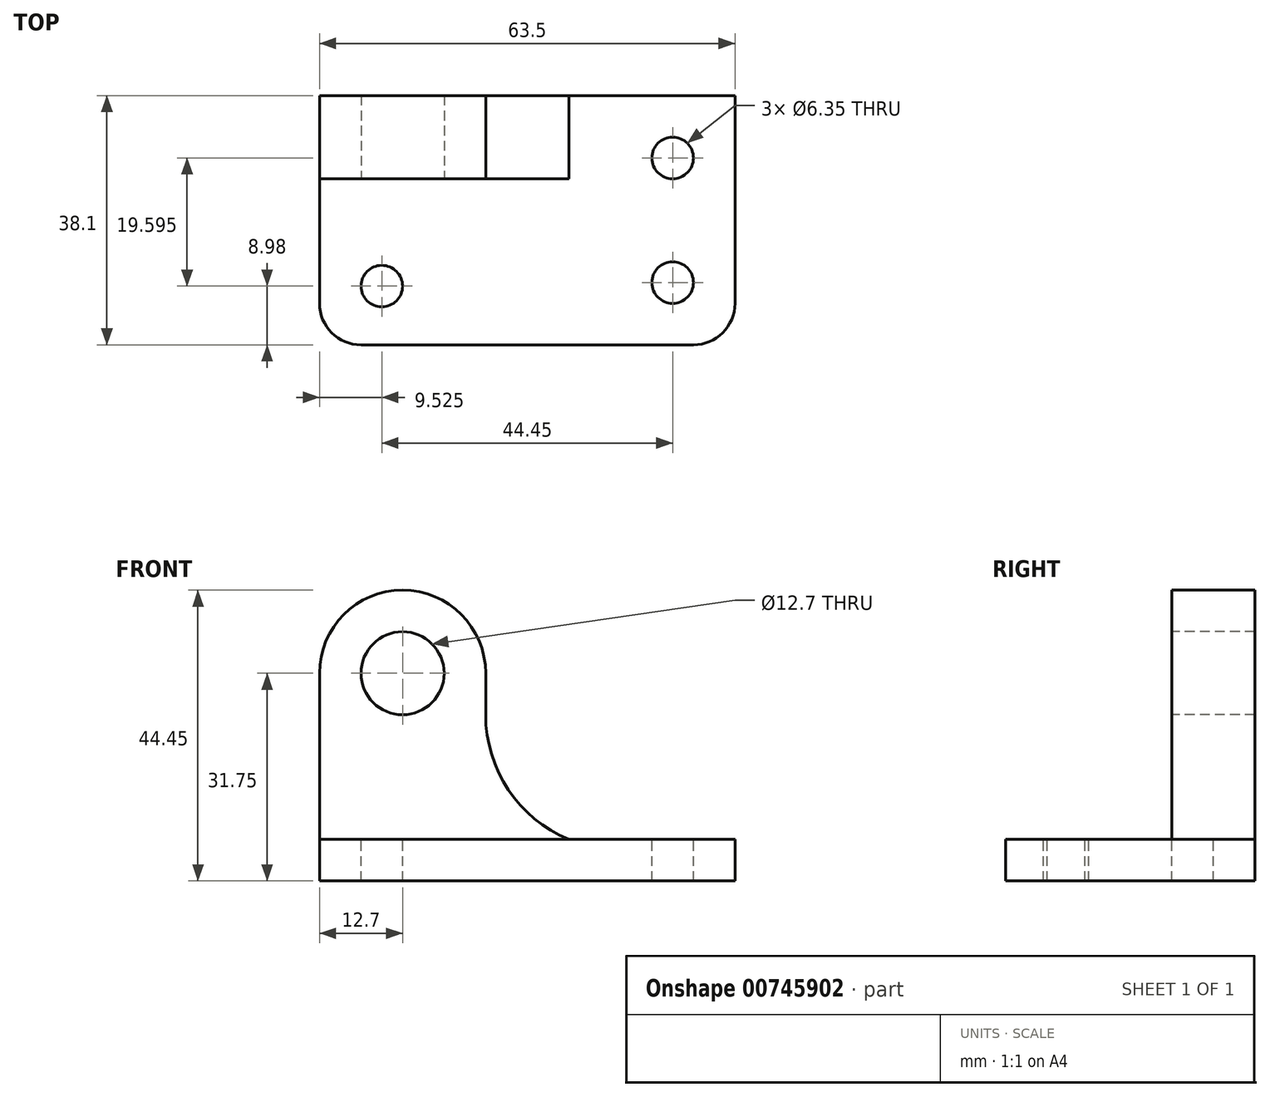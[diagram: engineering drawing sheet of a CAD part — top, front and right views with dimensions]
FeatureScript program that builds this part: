
annotation { "Feature Type Name" : "Feature", "Feature Type Description" : "" }
export const myFeature = defineFeature(function(context is Context, id is Id, definition is map)
    precondition{}
    {
        {
            var Q0;
            Q0=qCreatedBy(makeId("Top.planeOp"),FACE);
            var sketch = newSketch(context, id + "F0", { "sketchPlane" : qUnion([Q0])});
            skLineSegment(sketch, "E0", {"start": v(0, 0) * mm, "end": v(0, 6.35) * mm});
            skLineSegment(sketch, "E1", {"start": v(0, 6.35) * mm, "end": v(-6.35, 6.35) * mm});
            skLineSegment(sketch, "E2", {"start": v(-6.35, 6.35) * mm, "end": v(-6.35, 38.1) * mm});
            skLineSegment(sketch, "E3", {"start": v(-6.35, 38.1) * mm, "end": v(57.15, 38.1) * mm});
            skLineSegment(sketch, "E4", {"start": v(57.15, 38.1) * mm, "end": v(57.15, 6.35) * mm});
            skLineSegment(sketch, "E5", {"start": v(57.15, 6.35) * mm, "end": v(50.8, 6.35) * mm});
            skLineSegment(sketch, "E6", {"start": v(50.8, 6.35) * mm, "end": v(50.8, 0) * mm});
            skLineSegment(sketch, "E7", {"start": v(50.8, 0) * mm, "end": v(0, 0) * mm});
            skArc(sketch, "E8", {"start": v(-6.35, 6.35) * mm, "mid": v(-4.5, 1.86) * mm, "end": v(0, 0) * mm});
            skArc(sketch, "E9", {"start": v(50.8, 0) * mm, "mid": v(55.3, 1.86) * mm, "end": v(57.15, 6.35) * mm});
            skSolve(sketch);
        }
        {
            var Q0;
            Q0=makeQuery(id+"F0.imprint","IMPRINT",FACE,{"disambiguationData":[TD([[makeQuery(id+"F0.imprint","IMPRINT",EDGE,{"derivedFrom":sQuery(id+"F0.wireOp",EDGE,"E0")}),-1.0]])]});
            var Q1;
            Q1=makeQuery(id+"F0.imprint","IMPRINT",FACE,{"disambiguationData":[TD([[makeQuery(id+"F0.imprint","IMPRINT",EDGE,{"derivedFrom":sQuery(id+"F0.wireOp",EDGE,"E5")}),1.0]])]});
            var Q2;
            Q2=makeQuery(id+"F0.imprint","IMPRINT",FACE,{"disambiguationData":[TD([[makeQuery(id+"F0.imprint","IMPRINT",EDGE,{"derivedFrom":sQuery(id+"F0.wireOp",EDGE,"E0")}),1.0]])]});
            extrude(context, id + "F1", {"entities" : qUnion([Q0, Q1, Q2]), "depth" : 6.35 * mm, "offsetDistance" : 25.4 * mm});
        }
        {
            var Q0;
            Q0=makeQuery(id+"F1.opExtrude","SWEPT_FACE",FACE,{"disambiguationData":[OSD([sQuery(id+"F0.wireOp",EDGE,"E3")])]});
            var sketch = newSketch(context, id + "F2", { "sketchPlane" : qUnion([Q0])});
            skLineSegment(sketch, "E10", {"start": v(6.35, 6.35) * mm, "end": v(6.35, 31.75) * mm});
            skLineSegment(sketch, "E11", {"start": v(6.35, 31.75) * mm, "end": v(-19.05, 31.75) * mm});
            skLineSegment(sketch, "E12", {"start": v(-19.05, 31.75) * mm, "end": v(-19.05, 6.35) * mm});
            skLineSegment(sketch, "E13", {"start": v(-19.05, 6.35) * mm, "end": v(6.35, 6.35) * mm});
            skArc(sketch, "E14", {"start": v(6.35, 31.75) * mm, "mid": v(-6.35, 44.45) * mm, "end": v(-19.05, 31.75) * mm});
            skSolve(sketch);
        }
        {
            var Q0;
            Q0=makeQuery(id+"F2.imprint","IMPRINT",FACE,{"disambiguationData":[TD([[makeQuery(id+"F2.imprint","IMPRINT",EDGE,{"derivedFrom":sQuery(id+"F2.wireOp",EDGE,"E10")}),1.0]])]});
            var Q1;
            Q1=makeQuery(id+"F2.imprint","IMPRINT",FACE,{"disambiguationData":[TD([[makeQuery(id+"F2.imprint","IMPRINT",EDGE,{"derivedFrom":sQuery(id+"F2.wireOp",EDGE,"E11")}),-1.0]])]});
            extrude(context, id + "F3", {"entities" : qUnion([Q0, Q1]), "operationType" : NewBodyOperationType.ADD, "oppositeDirection" : true, "depth" : 12.7 * mm, "offsetDistance" : 25.4 * mm});
        }
        {
            var Q0;
            Q0=makeQuery(id+"F3.opExtrude","CAP_FACE",FACE,{"disambiguationData":[OSD([sQuery(id+"F2.wireOp",EDGE,"E10"),sQuery(id+"F2.wireOp",EDGE,"E12"),sQuery(id+"F2.wireOp",EDGE,"E13"),sQuery(id+"F2.wireOp",EDGE,"E14")])],"isStart":false});
            var sketch = newSketch(context, id + "F4", { "sketchPlane" : qUnion([Q0])});
            skCircle(sketch, "E15", {"center": v(6.35, 31.75) * mm, "radius": 6.35 * mm});
            skSolve(sketch);
        }
        {
            var Q0;
            Q0=makeQuery(id+"F4.imprint","IMPRINT",FACE,{"disambiguationData":[TD([[makeQuery(id+"F4.imprint","IMPRINT",EDGE,{"derivedFrom":sQuery(id+"F4.wireOp",EDGE,"E15")}),1.0]])]});
            extrude(context, id + "F5", {"entities" : qUnion([Q0]), "operationType" : NewBodyOperationType.REMOVE, "oppositeDirection" : true, "depth" : 25.4 * mm, "offsetDistance" : 25.4 * mm});
        }
        {
            var Q0;
            Q0=makeQuery(id+"F1.opExtrude","CAP_FACE",FACE,{"disambiguationData":[OSD([sQuery(id+"F0.wireOp",EDGE,"E2"),sQuery(id+"F0.wireOp",EDGE,"E3"),sQuery(id+"F0.wireOp",EDGE,"E4"),sQuery(id+"F0.wireOp",EDGE,"E7"),sQuery(id+"F0.wireOp",EDGE,"E8"),sQuery(id+"F0.wireOp",EDGE,"E9")])],"isStart":false});
            var sketch = newSketch(context, id + "F6", { "sketchPlane" : qUnion([Q0])});
            skCircle(sketch, "E16", {"center": v(3.17, 8.98) * mm, "radius": 3.18 * mm});
            skSolve(sketch);
        }
        {
            var Q0;
            Q0=makeQuery(id+"F6.imprint","IMPRINT",FACE,{"disambiguationData":[TD([[makeQuery(id+"F6.imprint","IMPRINT",EDGE,{"derivedFrom":sQuery(id+"F6.wireOp",EDGE,"E16")}),1.0]])]});
            extrude(context, id + "F7", {"entities" : qUnion([Q0]), "operationType" : NewBodyOperationType.REMOVE, "oppositeDirection" : true, "depth" : 25.4 * mm, "offsetDistance" : 25.4 * mm});
        }
        {
            var Q0;
            Q0=makeQuery(id+"F1.opExtrude","CAP_FACE",FACE,{"disambiguationData":[OSD([sQuery(id+"F0.wireOp",EDGE,"E2"),sQuery(id+"F0.wireOp",EDGE,"E3"),sQuery(id+"F0.wireOp",EDGE,"E4"),sQuery(id+"F0.wireOp",EDGE,"E7"),sQuery(id+"F0.wireOp",EDGE,"E8"),sQuery(id+"F0.wireOp",EDGE,"E9")])],"isStart":false});
            var sketch = newSketch(context, id + "F8", { "sketchPlane" : qUnion([Q0])});
            skCircle(sketch, "E17", {"center": v(47.63, 9.53) * mm, "radius": 3.18 * mm});
            skCircle(sketch, "E18", {"center": v(47.63, 28.57) * mm, "radius": 3.18 * mm});
            skSolve(sketch);
        }
        {
            var Q0;
            Q0=makeQuery(id+"F8.imprint","IMPRINT",FACE,{"disambiguationData":[TD([[makeQuery(id+"F8.imprint","IMPRINT",EDGE,{"derivedFrom":sQuery(id+"F8.wireOp",EDGE,"E18")}),1.0]])]});
            var Q1;
            Q1=makeQuery(id+"F8.imprint","IMPRINT",FACE,{"disambiguationData":[TD([[makeQuery(id+"F8.imprint","IMPRINT",EDGE,{"derivedFrom":sQuery(id+"F8.wireOp",EDGE,"E17")}),1.0]])]});
            extrude(context, id + "F9", {"entities" : qUnion([Q0, Q1]), "operationType" : NewBodyOperationType.REMOVE, "oppositeDirection" : true, "depth" : 25.4 * mm, "offsetDistance" : 25.4 * mm});
        }
        {
            var Q0;
            Q0=makeQuery(id+"F3.boolean.opBoolean","MERGE",FACE,{"derivedFrom":[makeQuery(id+"F1.opExtrude","SWEPT_FACE",FACE,{"disambiguationData":[OSD([sQuery(id+"F0.wireOp",EDGE,"E3")])]}),makeQuery(id+"F3.opExtrude","CAP_FACE",FACE,{"disambiguationData":[OSD([sQuery(id+"F2.wireOp",EDGE,"E10"),sQuery(id+"F2.wireOp",EDGE,"E12"),sQuery(id+"F2.wireOp",EDGE,"E13"),sQuery(id+"F2.wireOp",EDGE,"E14")])],"isStart":true})]});
            var sketch = newSketch(context, id + "F10", { "sketchPlane" : qUnion([Q0])});
            skLineSegment(sketch, "E19.bottom", {"start": v(-19.05, 25.4) * mm, "end": v(-31.75, 25.4) * mm});
            skLineSegment(sketch, "E19.top", {"start": v(-19.05, 6.35) * mm, "end": v(-31.75, 6.35) * mm});
            skLineSegment(sketch, "E19.left", {"start": v(-19.05, 25.4) * mm, "end": v(-19.05, 6.35) * mm});
            skLineSegment(sketch, "E19.right", {"start": v(-31.75, 25.4) * mm, "end": v(-31.75, 6.35) * mm});
            skSolve(sketch);
        }
        {
            var Q0;
            Q0=makeQuery(id+"F10.imprint","IMPRINT",FACE,{"disambiguationData":[TD([[makeQuery(id+"F10.imprint","IMPRINT",EDGE,{"derivedFrom":sQuery(id+"F10.wireOp",EDGE,"E19.bottom")}),1.0]])]});
            extrude(context, id + "F11", {"entities" : qUnion([Q0]), "operationType" : NewBodyOperationType.ADD, "oppositeDirection" : true, "depth" : 12.7 * mm, "offsetDistance" : 25.4 * mm});
        }
        {
            var Q0;
            Q0=makeQuery(id+"F11.boolean.opBoolean","MERGE",FACE,{"derivedFrom":[makeQuery(id+"F3.boolean.opBoolean","MERGE",FACE,{"derivedFrom":[makeQuery(id+"F1.opExtrude","SWEPT_FACE",FACE,{"disambiguationData":[OSD([sQuery(id+"F0.wireOp",EDGE,"E3")])]}),makeQuery(id+"F3.opExtrude","CAP_FACE",FACE,{"disambiguationData":[OSD([sQuery(id+"F2.wireOp",EDGE,"E10"),sQuery(id+"F2.wireOp",EDGE,"E12"),sQuery(id+"F2.wireOp",EDGE,"E13"),sQuery(id+"F2.wireOp",EDGE,"E14")])],"isStart":true})]}),makeQuery(id+"F11.opExtrude","CAP_FACE",FACE,{"disambiguationData":[OSD([sQuery(id+"F10.wireOp",EDGE,"E19.bottom"),sQuery(id+"F10.wireOp",EDGE,"E19.top"),sQuery(id+"F10.wireOp",EDGE,"E19.left"),sQuery(id+"F10.wireOp",EDGE,"E19.right")])],"isStart":true})]});
            var sketch = newSketch(context, id + "F12", { "sketchPlane" : qUnion([Q0])});
            skArc(sketch, "E20", {"start": v(-31.75, 6.35) * mm, "mid": v(-22.52, 13.95) * mm, "end": v(-19.05, 25.4) * mm});
            skSolve(sketch);
        }
        {
            var Q0;
            Q0=makeQuery(id+"F12.imprint","IMPRINT",FACE,{"disambiguationData":[TD([[makeQuery(id+"F12.imprint","IMPRINT",EDGE,{"derivedFrom":sQuery(id+"F12.wireOp",EDGE,"E20")}),1.0]])]});
            extrude(context, id + "F13", {"entities" : qUnion([Q0]), "operationType" : NewBodyOperationType.REMOVE, "oppositeDirection" : true, "depth" : 25.4 * mm, "offsetDistance" : 25.4 * mm});
        }
    });
